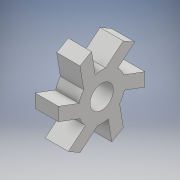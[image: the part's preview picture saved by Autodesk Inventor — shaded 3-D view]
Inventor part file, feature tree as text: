
AUTODESK INVENTOR PART (.ipt)
format: ipt  version: 2018 (Build 220112000, 112)  size: 276,992 bytes
history: native  units: mm
features: extrude x2, sketch x2, pattern_circular x1
ambient origin geometry x8: Origin, YZ Plane, XZ Plane, XY Plane, X Axis, Y Axis, Z Axis, Center Point
bodies: Solid1 (feature_tree)
feature tree (5):
  extrude  "Extrusion1"  Depth=3.5mm
  extrude  "Extrusion2"  Depth=3.5mm
  pattern_circular  "Circular Pattern1"  [2 undecoded]
  sketch  "Sketch1"  dims[d0=3.5mm d1=7.0mm]
  sketch  "Sketch2"  dims[d2=3.5mm d3=0.0mm d4=1.0mm d5=1.5mm d6=3.0mm d7=3.0mm d8=2.0mm d9=3.5mm d10=0.0mm d11=60.0mm d12=360.0deg]
note: 2 required parameter values undecoded (feature->parameter linkage not recoverable at this tier; creation-order binding heuristic only, values carry confidence <= 0.55)
